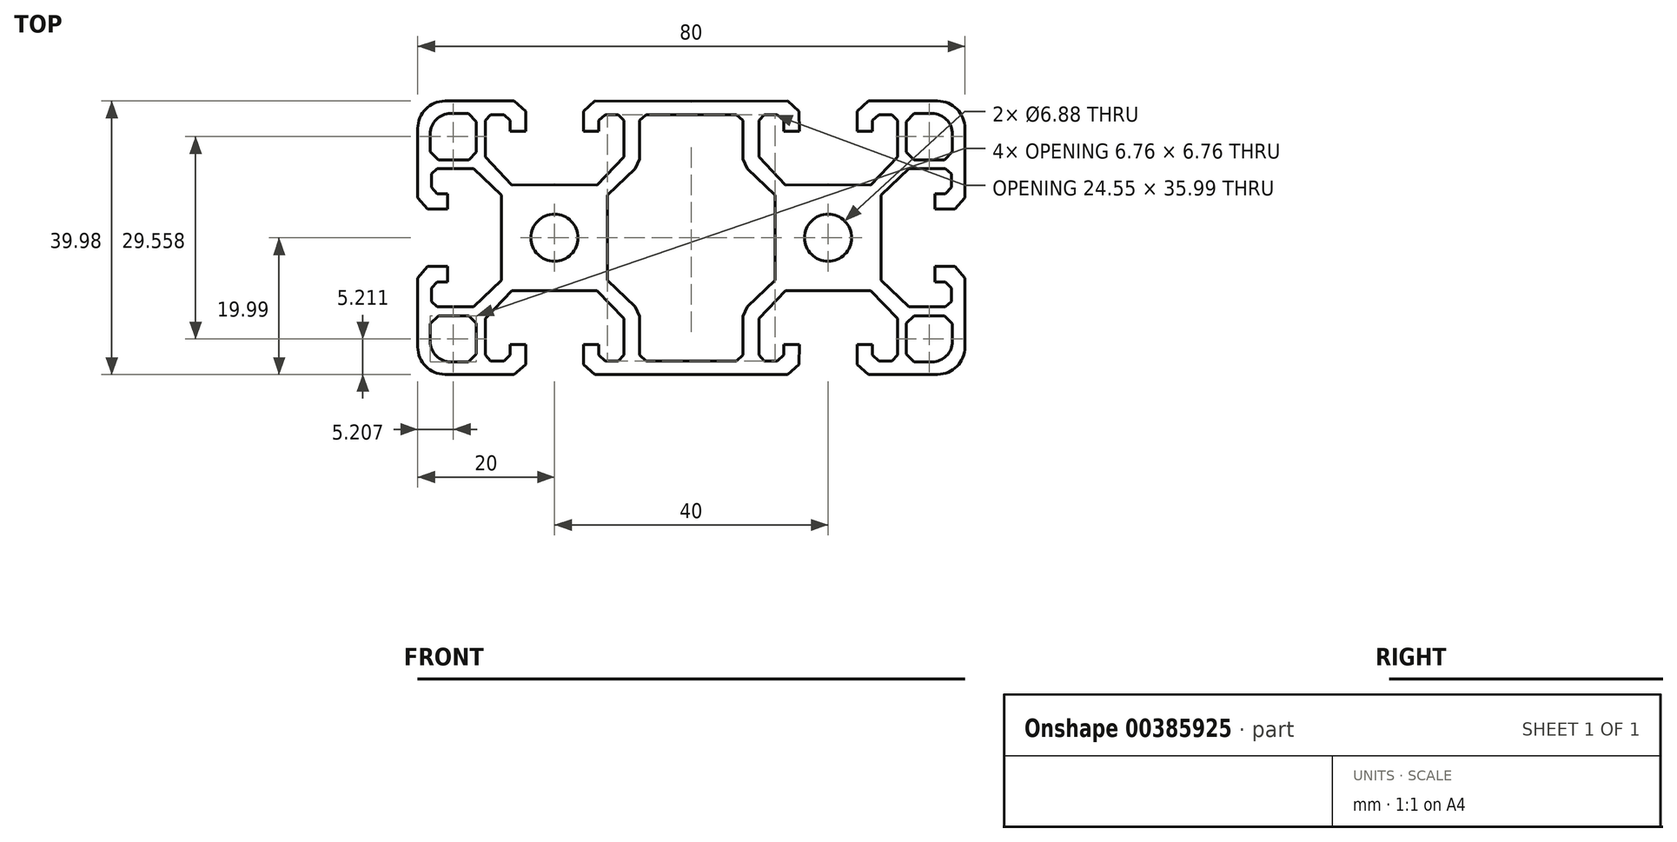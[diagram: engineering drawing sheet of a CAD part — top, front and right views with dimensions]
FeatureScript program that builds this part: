
annotation { "Feature Type Name" : "Feature", "Feature Type Description" : "" }
export const myFeature = defineFeature(function(context is Context, id is Id, definition is map)
    precondition{}
    {
        {
            var Q0;
            Q0=qCreatedBy(makeId("Top.planeOp"),FACE);
            var sketch = newSketch(context, id + "F0", { "sketchPlane" : qUnion([Q0])});
            skLineSegment(sketch, "E0", {"start": v(-150.5, 22.08) * mm, "end": v(-150.5, 75.17) * mm});
            skLineSegment(sketch, "E1", {"start": v(-104.33, 23.38) * mm, "end": v(-104.33, -0.03) * mm});
            skLineSegment(sketch, "E2", {"start": v(-104.33, 23.38) * mm, "end": v(-119.7, 38.04) * mm});
            skLineSegment(sketch, "E3", {"start": v(-119.7, 38.04) * mm, "end": v(-139.74, 38.04) * mm});
            skLineSegment(sketch, "E4", {"start": v(-139.74, 38.04) * mm, "end": v(-143, 35.05) * mm});
            skLineSegment(sketch, "E5", {"start": v(-143, 35.05) * mm, "end": v(-143, 27.8) * mm});
            skLineSegment(sketch, "E6", {"start": v(-143, 27.8) * mm, "end": v(-139.74, 24.28) * mm});
            skLineSegment(sketch, "E7", {"start": v(-139.74, 24.28) * mm, "end": v(-133.95, 24.28) * mm});
            skLineSegment(sketch, "E8", {"start": v(-133.95, 24.28) * mm, "end": v(-133.95, 15.85) * mm});
            skLineSegment(sketch, "E9", {"start": v(-133.95, 15.85) * mm, "end": v(-144.95, 15.85) * mm});
            skLineSegment(sketch, "E10", {"start": v(-144.95, 15.85) * mm, "end": v(-150.5, 22.08) * mm});
            skLineSegment(sketch, "E11", {"start": v(-75.25, 29.07) * mm, "end": v(-75.25, 12.95) * mm, "construction": true});
            skPoint(sketch, "E12", {"position": v(-75.25, 0) * mm});
            skCircle(sketch, "E13", {"center": v(-75.25, 0) * mm, "radius": 12.95 * mm});
            skLineSegment(sketch, "E14", {"start": v(-75.25, 0) * mm, "end": v(-150.5, 75.17) * mm, "construction": true});
            skLineSegment(sketch, "E15", {"start": v(-75.25, 0) * mm, "end": v(-175.7, 0) * mm, "construction": true});
            skLineSegment(sketch, "E16.MirrorCS", {"start": v(-97.41, 75.23) * mm, "end": v(-150.5, 75.17) * mm});
            skLineSegment(sketch, "E17.MirrorCS", {"start": v(-91.18, 69.68) * mm, "end": v(-97.41, 75.23) * mm});
            skLineSegment(sketch, "E18.MirrorCS", {"start": v(-91.17, 58.68) * mm, "end": v(-91.18, 69.68) * mm});
            skLineSegment(sketch, "E19.MirrorCS", {"start": v(-99.6, 58.67) * mm, "end": v(-91.17, 58.68) * mm});
            skLineSegment(sketch, "E20.MirrorCS", {"start": v(-99.6, 64.46) * mm, "end": v(-99.6, 58.67) * mm});
            skLineSegment(sketch, "E21.MirrorCS", {"start": v(-103.12, 67.72) * mm, "end": v(-99.6, 64.46) * mm});
            skLineSegment(sketch, "E22.MirrorCS", {"start": v(-110.38, 67.7) * mm, "end": v(-103.12, 67.72) * mm});
            skLineSegment(sketch, "E23.MirrorCS", {"start": v(-113.37, 64.44) * mm, "end": v(-110.38, 67.7) * mm});
            skLineSegment(sketch, "E24.MirrorCS", {"start": v(-113.34, 44.4) * mm, "end": v(-113.37, 64.44) * mm});
            skLineSegment(sketch, "E25.MirrorCS", {"start": v(-98.66, 29.05) * mm, "end": v(-113.34, 44.4) * mm});
            skLineSegment(sketch, "E26.MirrorCS", {"start": v(-98.66, 29.05) * mm, "end": v(-75.25, 29.07) * mm});
            skLineSegment(sketch, "E27.MirrorCS", {"start": v(-139.74, -38.04) * mm, "end": v(-143, -35.05) * mm});
            skLineSegment(sketch, "E28.MirrorCS", {"start": v(-143, -27.8) * mm, "end": v(-139.74, -24.28) * mm});
            skLineSegment(sketch, "E29.MirrorCS", {"start": v(-139.74, -24.28) * mm, "end": v(-133.95, -24.28) * mm});
            skLineSegment(sketch, "E30.MirrorCS", {"start": v(-144.95, -15.85) * mm, "end": v(-150.5, -22.08) * mm});
            skLineSegment(sketch, "E31.MirrorCS", {"start": v(-104.33, -23.38) * mm, "end": v(-119.7, -38.04) * mm});
            skLineSegment(sketch, "E32.MirrorCS", {"start": v(-97.41, -75.23) * mm, "end": v(-150.5, -75.17) * mm});
            skLineSegment(sketch, "E33.MirrorCS", {"start": v(-119.7, -38.04) * mm, "end": v(-139.74, -38.04) * mm});
            skLineSegment(sketch, "E34.MirrorCS", {"start": v(-150.5, -22.08) * mm, "end": v(-150.5, -75.17) * mm});
            skLineSegment(sketch, "E35.MirrorCS", {"start": v(-133.95, -24.28) * mm, "end": v(-133.95, -15.85) * mm});
            skLineSegment(sketch, "E36.MirrorCS", {"start": v(-143, -35.05) * mm, "end": v(-143, -27.8) * mm});
            skLineSegment(sketch, "E37.MirrorCS", {"start": v(-75.25, 0) * mm, "end": v(-150.5, -75.17) * mm, "construction": true});
            skLineSegment(sketch, "E38.MirrorCS", {"start": v(-133.95, -15.85) * mm, "end": v(-144.95, -15.85) * mm});
            skLineSegment(sketch, "E39.MirrorCS", {"start": v(-99.6, -64.46) * mm, "end": v(-99.6, -58.67) * mm});
            skLineSegment(sketch, "E40.MirrorCS", {"start": v(-113.37, -64.44) * mm, "end": v(-110.38, -67.7) * mm});
            skLineSegment(sketch, "E41.MirrorCS", {"start": v(-103.12, -67.72) * mm, "end": v(-99.6, -64.46) * mm});
            skLineSegment(sketch, "E42.MirrorCS", {"start": v(-98.66, -29.05) * mm, "end": v(-75.25, -29.07) * mm});
            skLineSegment(sketch, "E43.MirrorCS", {"start": v(-99.6, -58.67) * mm, "end": v(-91.17, -58.68) * mm});
            skLineSegment(sketch, "E44.MirrorCS", {"start": v(-91.18, -69.68) * mm, "end": v(-97.41, -75.23) * mm});
            skLineSegment(sketch, "E45.MirrorCS", {"start": v(-98.66, -29.05) * mm, "end": v(-113.34, -44.4) * mm});
            skLineSegment(sketch, "E46.MirrorCS", {"start": v(-110.38, -67.7) * mm, "end": v(-103.12, -67.72) * mm});
            skLineSegment(sketch, "E47.MirrorCS", {"start": v(-91.17, -58.68) * mm, "end": v(-91.18, -69.68) * mm});
            skLineSegment(sketch, "E48.MirrorCS", {"start": v(-113.34, -44.4) * mm, "end": v(-113.37, -64.44) * mm});
            skLineSegment(sketch, "E49.MirrorCS", {"start": v(-51.84, 29.05) * mm, "end": v(-75.25, 29.07) * mm});
            skLineSegment(sketch, "E50.MirrorCS", {"start": v(-51.84, 29.05) * mm, "end": v(-37.16, 44.4) * mm});
            skLineSegment(sketch, "E51.MirrorCS", {"start": v(-37.16, 44.4) * mm, "end": v(-37.14, 64.44) * mm});
            skLineSegment(sketch, "E52.MirrorCS", {"start": v(-40.13, 67.7) * mm, "end": v(-47.39, 67.72) * mm});
            skLineSegment(sketch, "E53.MirrorCS", {"start": v(-47.39, 67.72) * mm, "end": v(-50.9, 64.46) * mm});
            skLineSegment(sketch, "E54.MirrorCS", {"start": v(-59.33, 69.68) * mm, "end": v(-53.1, 75.23) * mm});
            skLineSegment(sketch, "E55.MirrorCS", {"start": v(-50.91, 58.67) * mm, "end": v(-59.34, 58.68) * mm});
            skLineSegment(sketch, "E56.MirrorCS", {"start": v(-53.1, 75.23) * mm, "end": v(0, 75.17) * mm});
            skLineSegment(sketch, "E57.MirrorCS", {"start": v(-59.34, 58.68) * mm, "end": v(-59.33, 69.68) * mm});
            skLineSegment(sketch, "E58.MirrorCS", {"start": v(-50.9, 64.46) * mm, "end": v(-50.91, 58.67) * mm});
            skLineSegment(sketch, "E59.MirrorCS", {"start": v(-37.14, 64.44) * mm, "end": v(-40.13, 67.7) * mm});
            skLineSegment(sketch, "E60.MirrorCS", {"start": v(-51.84, -29.05) * mm, "end": v(-75.25, -29.07) * mm});
            skLineSegment(sketch, "E61.MirrorCS", {"start": v(-51.84, -29.05) * mm, "end": v(-37.16, -44.4) * mm});
            skLineSegment(sketch, "E62.MirrorCS", {"start": v(-37.16, -44.4) * mm, "end": v(-37.14, -64.44) * mm});
            skLineSegment(sketch, "E63.MirrorCS", {"start": v(-37.14, -64.44) * mm, "end": v(-40.13, -67.7) * mm});
            skLineSegment(sketch, "E64.MirrorCS", {"start": v(-40.13, -67.7) * mm, "end": v(-47.39, -67.72) * mm});
            skLineSegment(sketch, "E65.MirrorCS", {"start": v(-47.39, -67.72) * mm, "end": v(-50.9, -64.46) * mm});
            skLineSegment(sketch, "E66.MirrorCS", {"start": v(-50.9, -64.46) * mm, "end": v(-50.91, -58.67) * mm});
            skLineSegment(sketch, "E67.MirrorCS", {"start": v(-50.91, -58.67) * mm, "end": v(-59.34, -58.68) * mm});
            skLineSegment(sketch, "E68.MirrorCS", {"start": v(-59.34, -58.68) * mm, "end": v(-59.33, -69.68) * mm});
            skLineSegment(sketch, "E69.MirrorCS", {"start": v(-59.33, -69.68) * mm, "end": v(-53.1, -75.23) * mm});
            skLineSegment(sketch, "E70.MirrorCS", {"start": v(-53.1, -75.23) * mm, "end": v(0, -75.17) * mm});
            skLineSegment(sketch, "E71", {"start": v(-120.32, 45.02) * mm, "end": v(-122.44, 42.9) * mm});
            skLineSegment(sketch, "E72", {"start": v(-122.44, 42.9) * mm, "end": v(-139.2, 42.9) * mm});
            skLineSegment(sketch, "E73", {"start": v(-139.2, 42.9) * mm, "end": v(-143.63, 47.32) * mm});
            skLineSegment(sketch, "E74", {"start": v(-143.63, 47.32) * mm, "end": v(-143.63, 68.3) * mm});
            skLineSegment(sketch, "E75.MirrorCS", {"start": v(-120.32, 45.02) * mm, "end": v(-118.2, 47.14) * mm});
            skLineSegment(sketch, "E76.MirrorCS", {"start": v(-118.2, 47.14) * mm, "end": v(-118.22, 63.9) * mm});
            skLineSegment(sketch, "E77.MirrorCS", {"start": v(-118.22, 63.9) * mm, "end": v(-122.65, 68.32) * mm});
            skLineSegment(sketch, "E78.MirrorCS", {"start": v(-122.65, 68.32) * mm, "end": v(-143.63, 68.3) * mm});
            skLineSegment(sketch, "E79.MirrorCS", {"start": v(-122.44, -42.9) * mm, "end": v(-139.2, -42.9) * mm});
            skLineSegment(sketch, "E80.MirrorCS", {"start": v(-120.32, -45.02) * mm, "end": v(-122.44, -42.9) * mm});
            skLineSegment(sketch, "E81.MirrorCS", {"start": v(-120.32, -45.02) * mm, "end": v(-118.2, -47.14) * mm});
            skLineSegment(sketch, "E82.MirrorCS", {"start": v(-118.2, -47.14) * mm, "end": v(-118.22, -63.9) * mm});
            skLineSegment(sketch, "E83.MirrorCS", {"start": v(-118.22, -63.9) * mm, "end": v(-122.65, -68.32) * mm});
            skLineSegment(sketch, "E84.MirrorCS", {"start": v(-122.65, -68.32) * mm, "end": v(-143.63, -68.3) * mm});
            skLineSegment(sketch, "E85.MirrorCS", {"start": v(-143.63, -47.32) * mm, "end": v(-143.63, -68.3) * mm});
            skLineSegment(sketch, "E86.MirrorCS", {"start": v(-139.2, -42.9) * mm, "end": v(-143.63, -47.32) * mm});
            skLineSegment(sketch, "E87.MirrorCS", {"start": v(-104.33, -23.38) * mm, "end": v(-104.33, 0.03) * mm});
            skLineSegment(sketch, "E88", {"start": v(0, 75.17) * mm, "end": v(0, -75.17) * mm, "construction": true});
            skLineSegment(sketch, "E89.MirrorCS", {"start": v(-46.18, 23.38) * mm, "end": v(-30.82, 38.04) * mm});
            skLineSegment(sketch, "E90.MirrorCS", {"start": v(-46.18, 23.38) * mm, "end": v(-46.18, -0.03) * mm});
            skLineSegment(sketch, "E91.MirrorCS", {"start": v(-46.18, -23.38) * mm, "end": v(-46.18, 0.03) * mm});
            skLineSegment(sketch, "E92.MirrorCS", {"start": v(-46.18, -23.38) * mm, "end": v(-30.82, -38.04) * mm});
            skLineSegment(sketch, "E93", {"start": v(-30.82, 38.04) * mm, "end": v(-28.34, 43.24) * mm});
            skLineSegment(sketch, "E94", {"start": v(-28.34, 43.24) * mm, "end": v(-28.34, 64.44) * mm});
            skLineSegment(sketch, "E95", {"start": v(-28.34, 64.44) * mm, "end": v(-24.77, 67.7) * mm});
            skLineSegment(sketch, "E96", {"start": v(-24.77, 67.7) * mm, "end": v(0, 67.7) * mm});
            skLineSegment(sketch, "E97.MirrorCS", {"start": v(-30.82, -38.04) * mm, "end": v(-28.34, -43.24) * mm});
            skLineSegment(sketch, "E98.MirrorCS", {"start": v(-28.34, -43.24) * mm, "end": v(-28.34, -64.44) * mm});
            skLineSegment(sketch, "E99.MirrorCS", {"start": v(-24.77, -67.7) * mm, "end": v(0, -67.7) * mm});
            skLineSegment(sketch, "E100.MirrorCS", {"start": v(-28.34, -64.44) * mm, "end": v(-24.77, -67.7) * mm});
            skLineSegment(sketch, "E101.MirrorCS", {"start": v(139.74, -38.04) * mm, "end": v(143, -35.05) * mm});
            skLineSegment(sketch, "E102.MirrorCS", {"start": v(50.9, -64.46) * mm, "end": v(50.91, -58.67) * mm});
            skLineSegment(sketch, "E103.MirrorCS", {"start": v(110.38, 67.7) * mm, "end": v(103.12, 67.72) * mm});
            skLineSegment(sketch, "E104.MirrorCS", {"start": v(30.82, -38.04) * mm, "end": v(28.34, -43.24) * mm});
            skLineSegment(sketch, "E105.MirrorCS", {"start": v(120.32, 45.02) * mm, "end": v(118.2, 47.14) * mm});
            skLineSegment(sketch, "E106.MirrorCS", {"start": v(37.14, 64.44) * mm, "end": v(40.13, 67.7) * mm});
            skLineSegment(sketch, "E107.MirrorCS", {"start": v(50.9, 64.46) * mm, "end": v(50.91, 58.67) * mm});
            skLineSegment(sketch, "E108.MirrorCS", {"start": v(103.12, 67.72) * mm, "end": v(99.6, 64.46) * mm});
            skLineSegment(sketch, "E109.MirrorCS", {"start": v(120.32, -45.02) * mm, "end": v(118.2, -47.14) * mm});
            skLineSegment(sketch, "E110.MirrorCS", {"start": v(139.2, 42.9) * mm, "end": v(143.63, 47.32) * mm});
            skLineSegment(sketch, "E111.MirrorCS", {"start": v(40.13, 67.7) * mm, "end": v(47.39, 67.72) * mm});
            skLineSegment(sketch, "E112.MirrorCS", {"start": v(139.74, 24.28) * mm, "end": v(133.95, 24.28) * mm});
            skLineSegment(sketch, "E113.MirrorCS", {"start": v(139.2, -42.9) * mm, "end": v(143.63, -47.32) * mm});
            skLineSegment(sketch, "E114.MirrorCS", {"start": v(103.12, -67.72) * mm, "end": v(99.6, -64.46) * mm});
            skLineSegment(sketch, "E115.MirrorCS", {"start": v(144.95, -15.85) * mm, "end": v(150.5, -22.08) * mm});
            skLineSegment(sketch, "E116.MirrorCS", {"start": v(59.33, 69.68) * mm, "end": v(53.1, 75.23) * mm});
            skLineSegment(sketch, "E117.MirrorCS", {"start": v(139.74, -24.28) * mm, "end": v(133.95, -24.28) * mm});
            skLineSegment(sketch, "E118.MirrorCS", {"start": v(143, 27.8) * mm, "end": v(139.74, 24.28) * mm});
            skLineSegment(sketch, "E119.MirrorCS", {"start": v(118.22, 63.9) * mm, "end": v(122.65, 68.32) * mm});
            skLineSegment(sketch, "E120.MirrorCS", {"start": v(110.38, -67.7) * mm, "end": v(103.12, -67.72) * mm});
            skLineSegment(sketch, "E121.MirrorCS", {"start": v(143, -35.05) * mm, "end": v(143, -27.8) * mm});
            skLineSegment(sketch, "E122.MirrorCS", {"start": v(120.32, -45.02) * mm, "end": v(122.44, -42.9) * mm});
            skLineSegment(sketch, "E123.MirrorCS", {"start": v(99.6, 64.46) * mm, "end": v(99.6, 58.67) * mm});
            skLineSegment(sketch, "E124.MirrorCS", {"start": v(40.13, -67.7) * mm, "end": v(47.39, -67.72) * mm});
            skLineSegment(sketch, "E125.MirrorCS", {"start": v(47.39, -67.72) * mm, "end": v(50.9, -64.46) * mm});
            skLineSegment(sketch, "E126.MirrorCS", {"start": v(91.18, 69.68) * mm, "end": v(97.41, 75.23) * mm});
            skLineSegment(sketch, "E127.MirrorCS", {"start": v(28.34, 64.44) * mm, "end": v(24.77, 67.7) * mm});
            skLineSegment(sketch, "E128.MirrorCS", {"start": v(113.37, -64.44) * mm, "end": v(110.38, -67.7) * mm});
            skLineSegment(sketch, "E129.MirrorCS", {"start": v(37.14, -64.44) * mm, "end": v(40.13, -67.7) * mm});
            skLineSegment(sketch, "E130.MirrorCS", {"start": v(144.95, 15.85) * mm, "end": v(150.5, 22.08) * mm});
            skLineSegment(sketch, "E131.MirrorCS", {"start": v(91.18, -69.68) * mm, "end": v(97.41, -75.23) * mm});
            skLineSegment(sketch, "E132.MirrorCS", {"start": v(143, 35.05) * mm, "end": v(143, 27.8) * mm});
            skLineSegment(sketch, "E133.MirrorCS", {"start": v(133.95, 24.28) * mm, "end": v(133.95, 15.85) * mm});
            skLineSegment(sketch, "E134.MirrorCS", {"start": v(99.6, -64.46) * mm, "end": v(99.6, -58.67) * mm});
            skLineSegment(sketch, "E135.MirrorCS", {"start": v(59.33, -69.68) * mm, "end": v(53.1, -75.23) * mm});
            skLineSegment(sketch, "E136.MirrorCS", {"start": v(139.74, 38.04) * mm, "end": v(143, 35.05) * mm});
            skLineSegment(sketch, "E137.MirrorCS", {"start": v(47.39, 67.72) * mm, "end": v(50.9, 64.46) * mm});
            skLineSegment(sketch, "E138.MirrorCS", {"start": v(99.6, -58.67) * mm, "end": v(91.17, -58.68) * mm});
            skLineSegment(sketch, "E139.MirrorCS", {"start": v(113.37, 64.44) * mm, "end": v(110.38, 67.7) * mm});
            skLineSegment(sketch, "E140.MirrorCS", {"start": v(50.91, -58.67) * mm, "end": v(59.34, -58.68) * mm});
            skLineSegment(sketch, "E141.MirrorCS", {"start": v(30.82, 38.04) * mm, "end": v(28.34, 43.24) * mm});
            skLineSegment(sketch, "E142.MirrorCS", {"start": v(120.32, 45.02) * mm, "end": v(122.44, 42.9) * mm});
            skLineSegment(sketch, "E143.MirrorCS", {"start": v(99.6, 58.67) * mm, "end": v(91.17, 58.68) * mm});
            skLineSegment(sketch, "E144.MirrorCS", {"start": v(143, -27.8) * mm, "end": v(139.74, -24.28) * mm});
            skLineSegment(sketch, "E145.MirrorCS", {"start": v(28.34, -64.44) * mm, "end": v(24.77, -67.7) * mm});
            skLineSegment(sketch, "E146.MirrorCS", {"start": v(118.22, -63.9) * mm, "end": v(122.65, -68.32) * mm});
            skLineSegment(sketch, "E147.MirrorCS", {"start": v(133.95, -24.28) * mm, "end": v(133.95, -15.85) * mm});
            skLineSegment(sketch, "E148.MirrorCS", {"start": v(50.91, 58.67) * mm, "end": v(59.34, 58.68) * mm});
            skLineSegment(sketch, "E149.MirrorCS", {"start": v(104.33, -23.38) * mm, "end": v(119.7, -38.04) * mm});
            skLineSegment(sketch, "E150.MirrorCS", {"start": v(97.41, -75.23) * mm, "end": v(150.5, -75.17) * mm});
            skLineSegment(sketch, "E151.MirrorCS", {"start": v(75.25, 0) * mm, "end": v(150.5, -75.17) * mm, "construction": true});
            skLineSegment(sketch, "E152.MirrorCS", {"start": v(119.7, -38.04) * mm, "end": v(139.74, -38.04) * mm});
            skLineSegment(sketch, "E153.MirrorCS", {"start": v(104.33, -23.38) * mm, "end": v(104.33, 0.03) * mm});
            skLineSegment(sketch, "E154.MirrorCS", {"start": v(51.84, 29.05) * mm, "end": v(37.16, 44.4) * mm});
            skLineSegment(sketch, "E155.MirrorCS", {"start": v(133.95, -15.85) * mm, "end": v(144.95, -15.85) * mm});
            skLineSegment(sketch, "E156.MirrorCS", {"start": v(118.2, -47.14) * mm, "end": v(118.22, -63.9) * mm});
            skLineSegment(sketch, "E157.MirrorCS", {"start": v(75.25, 0) * mm, "end": v(175.7, 0) * mm, "construction": true});
            skPoint(sketch, "E158.MirrorP", {"position": v(75.25, 0) * mm});
            skLineSegment(sketch, "E159.MirrorCS", {"start": v(46.18, 23.38) * mm, "end": v(46.18, -0.03) * mm});
            skLineSegment(sketch, "E160.MirrorCS", {"start": v(98.66, -29.05) * mm, "end": v(113.34, -44.4) * mm});
            skLineSegment(sketch, "E161.MirrorCS", {"start": v(46.18, 23.38) * mm, "end": v(30.82, 38.04) * mm});
            skLineSegment(sketch, "E162.MirrorCS", {"start": v(143.63, 47.32) * mm, "end": v(143.63, 68.3) * mm});
            skLineSegment(sketch, "E163.MirrorCS", {"start": v(150.5, 22.08) * mm, "end": v(150.5, 75.17) * mm});
            skLineSegment(sketch, "E164.MirrorCS", {"start": v(28.34, -43.24) * mm, "end": v(28.34, -64.44) * mm});
            skLineSegment(sketch, "E165.MirrorCS", {"start": v(133.95, 15.85) * mm, "end": v(144.95, 15.85) * mm});
            skLineSegment(sketch, "E166.MirrorCS", {"start": v(104.33, 23.38) * mm, "end": v(104.33, -0.03) * mm});
            skLineSegment(sketch, "E167.MirrorCS", {"start": v(59.34, -58.68) * mm, "end": v(59.33, -69.68) * mm});
            skLineSegment(sketch, "E168.MirrorCS", {"start": v(98.66, 29.05) * mm, "end": v(75.25, 29.07) * mm});
            skCircle(sketch, "E169.MirrorC", {"center": v(75.25, 0) * mm, "radius": 12.95 * mm});
            skLineSegment(sketch, "E170.MirrorCS", {"start": v(91.17, -58.68) * mm, "end": v(91.18, -69.68) * mm});
            skLineSegment(sketch, "E171.MirrorCS", {"start": v(113.34, -44.4) * mm, "end": v(113.37, -64.44) * mm});
            skLineSegment(sketch, "E172.MirrorCS", {"start": v(46.18, -23.38) * mm, "end": v(30.82, -38.04) * mm});
            skLineSegment(sketch, "E173.MirrorCS", {"start": v(51.84, 29.05) * mm, "end": v(75.25, 29.07) * mm});
            skLineSegment(sketch, "E174.MirrorCS", {"start": v(75.25, 0) * mm, "end": v(150.5, 75.17) * mm, "construction": true});
            skLineSegment(sketch, "E175.MirrorCS", {"start": v(51.84, -29.05) * mm, "end": v(37.16, -44.4) * mm});
            skLineSegment(sketch, "E176.MirrorCS", {"start": v(24.77, -67.7) * mm, "end": v(0, -67.7) * mm});
            skLineSegment(sketch, "E177.MirrorCS", {"start": v(37.16, 44.4) * mm, "end": v(37.14, 64.44) * mm});
            skLineSegment(sketch, "E178.MirrorCS", {"start": v(51.84, -29.05) * mm, "end": v(75.25, -29.07) * mm});
            skLineSegment(sketch, "E179.MirrorCS", {"start": v(113.34, 44.4) * mm, "end": v(113.37, 64.44) * mm});
            skLineSegment(sketch, "E180.MirrorCS", {"start": v(24.77, 67.7) * mm, "end": v(0, 67.7) * mm});
            skLineSegment(sketch, "E181.MirrorCS", {"start": v(53.1, -75.23) * mm, "end": v(0, -75.17) * mm});
            skLineSegment(sketch, "E182.MirrorCS", {"start": v(75.25, 29.07) * mm, "end": v(75.25, 12.95) * mm, "construction": true});
            skLineSegment(sketch, "E183.MirrorCS", {"start": v(97.41, 75.23) * mm, "end": v(150.5, 75.17) * mm});
            skLineSegment(sketch, "E184.MirrorCS", {"start": v(122.65, -68.32) * mm, "end": v(143.63, -68.3) * mm});
            skLineSegment(sketch, "E185.MirrorCS", {"start": v(122.44, -42.9) * mm, "end": v(139.2, -42.9) * mm});
            skLineSegment(sketch, "E186.MirrorCS", {"start": v(98.66, -29.05) * mm, "end": v(75.25, -29.07) * mm});
            skLineSegment(sketch, "E187.MirrorCS", {"start": v(46.18, -23.38) * mm, "end": v(46.18, 0.03) * mm});
            skLineSegment(sketch, "E188.MirrorCS", {"start": v(91.17, 58.68) * mm, "end": v(91.18, 69.68) * mm});
            skLineSegment(sketch, "E189.MirrorCS", {"start": v(122.65, 68.32) * mm, "end": v(143.63, 68.3) * mm});
            skLineSegment(sketch, "E190.MirrorCS", {"start": v(59.34, 58.68) * mm, "end": v(59.33, 69.68) * mm});
            skLineSegment(sketch, "E191.MirrorCS", {"start": v(53.1, 75.23) * mm, "end": v(0, 75.17) * mm});
            skLineSegment(sketch, "E192.MirrorCS", {"start": v(37.16, -44.4) * mm, "end": v(37.14, -64.44) * mm});
            skLineSegment(sketch, "E193.MirrorCS", {"start": v(104.33, 23.38) * mm, "end": v(119.7, 38.04) * mm});
            skLineSegment(sketch, "E194.MirrorCS", {"start": v(119.7, 38.04) * mm, "end": v(139.74, 38.04) * mm});
            skLineSegment(sketch, "E195.MirrorCS", {"start": v(28.34, 43.24) * mm, "end": v(28.34, 64.44) * mm});
            skLineSegment(sketch, "E196.MirrorCS", {"start": v(122.44, 42.9) * mm, "end": v(139.2, 42.9) * mm});
            skLineSegment(sketch, "E197.MirrorCS", {"start": v(118.2, 47.14) * mm, "end": v(118.22, 63.9) * mm});
            skLineSegment(sketch, "E198.MirrorCS", {"start": v(98.66, 29.05) * mm, "end": v(113.34, 44.4) * mm});
            skLineSegment(sketch, "E199.MirrorCS", {"start": v(150.5, -22.08) * mm, "end": v(150.5, -75.17) * mm});
            skLineSegment(sketch, "E200.MirrorCS", {"start": v(143.63, -47.32) * mm, "end": v(143.63, -68.3) * mm});
            skPoint(sketch, "E201.visualSharp", {"position": v(-150.5, 75.17) * mm});
            skLineSegment(sketch, "E201.filletArc", {"start": v(-575.32, 265.37) * mm, "end": v(-575.32, 265.37) * mm});
            skSolve(sketch);
        }
        {
            var Q0;
            Q0=makeQuery(id+"F0.imprint","IMPRINT",FACE,{"disambiguationData":[TD([[makeQuery(id+"F0.imprint","IMPRINT",EDGE,{"derivedFrom":sQuery(id+"F0.wireOp",EDGE,"E0")}),-1.0]])]});
            extrude(context, id + "F1", {"entities" : qUnion([Q0]), "depth" : 0 * mm, "offsetDistance" : 25 * mm});
        }
        {
            var Q0;
            Q0=makeQuery(id+"F1.opExtrude","SWEPT_BODY",BODY,{"disambiguationData":[OSD([sQuery(id+"F0.wireOp",EDGE,"E0"),sQuery(id+"F0.wireOp",EDGE,"E1"),sQuery(id+"F0.wireOp",EDGE,"E2"),sQuery(id+"F0.wireOp",EDGE,"E3"),sQuery(id+"F0.wireOp",EDGE,"E4"),sQuery(id+"F0.wireOp",EDGE,"E5"),sQuery(id+"F0.wireOp",EDGE,"E6"),sQuery(id+"F0.wireOp",EDGE,"E7"),sQuery(id+"F0.wireOp",EDGE,"E8"),sQuery(id+"F0.wireOp",EDGE,"E9"),sQuery(id+"F0.wireOp",EDGE,"E10"),sQuery(id+"F0.wireOp",EDGE,"E13"),sQuery(id+"F0.wireOp",EDGE,"E16.MirrorCS"),sQuery(id+"F0.wireOp",EDGE,"E17.MirrorCS"),sQuery(id+"F0.wireOp",EDGE,"E18.MirrorCS"),sQuery(id+"F0.wireOp",EDGE,"E19.MirrorCS"),sQuery(id+"F0.wireOp",EDGE,"E20.MirrorCS"),sQuery(id+"F0.wireOp",EDGE,"E21.MirrorCS"),sQuery(id+"F0.wireOp",EDGE,"E22.MirrorCS"),sQuery(id+"F0.wireOp",EDGE,"E23.MirrorCS"),sQuery(id+"F0.wireOp",EDGE,"E24.MirrorCS"),sQuery(id+"F0.wireOp",EDGE,"E25.MirrorCS"),sQuery(id+"F0.wireOp",EDGE,"E26.MirrorCS"),sQuery(id+"F0.wireOp",EDGE,"E27.MirrorCS"),sQuery(id+"F0.wireOp",EDGE,"E28.MirrorCS"),sQuery(id+"F0.wireOp",EDGE,"E29.MirrorCS"),sQuery(id+"F0.wireOp",EDGE,"E30.MirrorCS"),sQuery(id+"F0.wireOp",EDGE,"E34.MirrorCS"),sQuery(id+"F0.wireOp",EDGE,"E35.MirrorCS"),sQuery(id+"F0.wireOp",EDGE,"E36.MirrorCS"),sQuery(id+"F0.wireOp",EDGE,"E38.MirrorCS"),sQuery(id+"F0.wireOp",EDGE,"E39.MirrorCS"),sQuery(id+"F0.wireOp",EDGE,"E40.MirrorCS"),sQuery(id+"F0.wireOp",EDGE,"E33.MirrorCS"),sQuery(id+"F0.wireOp",EDGE,"E41.MirrorCS"),sQuery(id+"F0.wireOp",EDGE,"E42.MirrorCS"),sQuery(id+"F0.wireOp",EDGE,"E43.MirrorCS"),sQuery(id+"F0.wireOp",EDGE,"E44.MirrorCS"),sQuery(id+"F0.wireOp",EDGE,"E45.MirrorCS"),sQuery(id+"F0.wireOp",EDGE,"E46.MirrorCS"),sQuery(id+"F0.wireOp",EDGE,"E47.MirrorCS"),sQuery(id+"F0.wireOp",EDGE,"E32.MirrorCS"),sQuery(id+"F0.wireOp",EDGE,"E31.MirrorCS"),sQuery(id+"F0.wireOp",EDGE,"E48.MirrorCS"),sQuery(id+"F0.wireOp",EDGE,"E49.MirrorCS"),sQuery(id+"F0.wireOp",EDGE,"E50.MirrorCS"),sQuery(id+"F0.wireOp",EDGE,"E51.MirrorCS"),sQuery(id+"F0.wireOp",EDGE,"E52.MirrorCS"),sQuery(id+"F0.wireOp",EDGE,"E53.MirrorCS"),sQuery(id+"F0.wireOp",EDGE,"E54.MirrorCS"),sQuery(id+"F0.wireOp",EDGE,"E55.MirrorCS"),sQuery(id+"F0.wireOp",EDGE,"E56.MirrorCS"),sQuery(id+"F0.wireOp",EDGE,"E57.MirrorCS"),sQuery(id+"F0.wireOp",EDGE,"E58.MirrorCS"),sQuery(id+"F0.wireOp",EDGE,"E59.MirrorCS"),sQuery(id+"F0.wireOp",EDGE,"E60.MirrorCS"),sQuery(id+"F0.wireOp",EDGE,"E61.MirrorCS"),sQuery(id+"F0.wireOp",EDGE,"E62.MirrorCS"),sQuery(id+"F0.wireOp",EDGE,"E63.MirrorCS"),sQuery(id+"F0.wireOp",EDGE,"E64.MirrorCS"),sQuery(id+"F0.wireOp",EDGE,"E65.MirrorCS"),sQuery(id+"F0.wireOp",EDGE,"E66.MirrorCS"),sQuery(id+"F0.wireOp",EDGE,"E67.MirrorCS"),sQuery(id+"F0.wireOp",EDGE,"E68.MirrorCS"),sQuery(id+"F0.wireOp",EDGE,"E69.MirrorCS"),sQuery(id+"F0.wireOp",EDGE,"E70.MirrorCS"),sQuery(id+"F0.wireOp",EDGE,"E71"),sQuery(id+"F0.wireOp",EDGE,"E72"),sQuery(id+"F0.wireOp",EDGE,"E73"),sQuery(id+"F0.wireOp",EDGE,"E74"),sQuery(id+"F0.wireOp",EDGE,"E75.MirrorCS"),sQuery(id+"F0.wireOp",EDGE,"E76.MirrorCS"),sQuery(id+"F0.wireOp",EDGE,"E77.MirrorCS"),sQuery(id+"F0.wireOp",EDGE,"E78.MirrorCS"),sQuery(id+"F0.wireOp",EDGE,"E79.MirrorCS"),sQuery(id+"F0.wireOp",EDGE,"E80.MirrorCS"),sQuery(id+"F0.wireOp",EDGE,"E81.MirrorCS"),sQuery(id+"F0.wireOp",EDGE,"E82.MirrorCS"),sQuery(id+"F0.wireOp",EDGE,"E83.MirrorCS"),sQuery(id+"F0.wireOp",EDGE,"E84.MirrorCS"),sQuery(id+"F0.wireOp",EDGE,"E85.MirrorCS"),sQuery(id+"F0.wireOp",EDGE,"E86.MirrorCS"),sQuery(id+"F0.wireOp",EDGE,"E87.MirrorCS"),sQuery(id+"F0.wireOp",EDGE,"E89.MirrorCS"),sQuery(id+"F0.wireOp",EDGE,"E90.MirrorCS"),sQuery(id+"F0.wireOp",EDGE,"E91.MirrorCS"),sQuery(id+"F0.wireOp",EDGE,"E92.MirrorCS"),sQuery(id+"F0.wireOp",EDGE,"E93"),sQuery(id+"F0.wireOp",EDGE,"E94"),sQuery(id+"F0.wireOp",EDGE,"E95"),sQuery(id+"F0.wireOp",EDGE,"E96"),sQuery(id+"F0.wireOp",EDGE,"E97.MirrorCS"),sQuery(id+"F0.wireOp",EDGE,"E98.MirrorCS"),sQuery(id+"F0.wireOp",EDGE,"E99.MirrorCS"),sQuery(id+"F0.wireOp",EDGE,"E100.MirrorCS"),sQuery(id+"F0.wireOp",EDGE,"E101.MirrorCS"),sQuery(id+"F0.wireOp",EDGE,"E102.MirrorCS"),sQuery(id+"F0.wireOp",EDGE,"E103.MirrorCS"),sQuery(id+"F0.wireOp",EDGE,"E104.MirrorCS"),sQuery(id+"F0.wireOp",EDGE,"E105.MirrorCS"),sQuery(id+"F0.wireOp",EDGE,"E106.MirrorCS"),sQuery(id+"F0.wireOp",EDGE,"E107.MirrorCS"),sQuery(id+"F0.wireOp",EDGE,"E108.MirrorCS"),sQuery(id+"F0.wireOp",EDGE,"E109.MirrorCS"),sQuery(id+"F0.wireOp",EDGE,"E110.MirrorCS"),sQuery(id+"F0.wireOp",EDGE,"E111.MirrorCS"),sQuery(id+"F0.wireOp",EDGE,"E112.MirrorCS"),sQuery(id+"F0.wireOp",EDGE,"E113.MirrorCS"),sQuery(id+"F0.wireOp",EDGE,"E114.MirrorCS"),sQuery(id+"F0.wireOp",EDGE,"E115.MirrorCS"),sQuery(id+"F0.wireOp",EDGE,"E116.MirrorCS"),sQuery(id+"F0.wireOp",EDGE,"E117.MirrorCS"),sQuery(id+"F0.wireOp",EDGE,"E118.MirrorCS"),sQuery(id+"F0.wireOp",EDGE,"E119.MirrorCS"),sQuery(id+"F0.wireOp",EDGE,"E120.MirrorCS"),sQuery(id+"F0.wireOp",EDGE,"E121.MirrorCS"),sQuery(id+"F0.wireOp",EDGE,"E122.MirrorCS"),sQuery(id+"F0.wireOp",EDGE,"E123.MirrorCS"),sQuery(id+"F0.wireOp",EDGE,"E124.MirrorCS"),sQuery(id+"F0.wireOp",EDGE,"E125.MirrorCS"),sQuery(id+"F0.wireOp",EDGE,"E126.MirrorCS"),sQuery(id+"F0.wireOp",EDGE,"E127.MirrorCS"),sQuery(id+"F0.wireOp",EDGE,"E128.MirrorCS"),sQuery(id+"F0.wireOp",EDGE,"E129.MirrorCS"),sQuery(id+"F0.wireOp",EDGE,"E130.MirrorCS"),sQuery(id+"F0.wireOp",EDGE,"E131.MirrorCS"),sQuery(id+"F0.wireOp",EDGE,"E132.MirrorCS"),sQuery(id+"F0.wireOp",EDGE,"E133.MirrorCS"),sQuery(id+"F0.wireOp",EDGE,"E134.MirrorCS"),sQuery(id+"F0.wireOp",EDGE,"E135.MirrorCS"),sQuery(id+"F0.wireOp",EDGE,"E136.MirrorCS"),sQuery(id+"F0.wireOp",EDGE,"E137.MirrorCS"),sQuery(id+"F0.wireOp",EDGE,"E138.MirrorCS"),sQuery(id+"F0.wireOp",EDGE,"E139.MirrorCS"),sQuery(id+"F0.wireOp",EDGE,"E140.MirrorCS"),sQuery(id+"F0.wireOp",EDGE,"E141.MirrorCS"),sQuery(id+"F0.wireOp",EDGE,"E142.MirrorCS"),sQuery(id+"F0.wireOp",EDGE,"E143.MirrorCS"),sQuery(id+"F0.wireOp",EDGE,"E144.MirrorCS"),sQuery(id+"F0.wireOp",EDGE,"E145.MirrorCS"),sQuery(id+"F0.wireOp",EDGE,"E146.MirrorCS"),sQuery(id+"F0.wireOp",EDGE,"E147.MirrorCS"),sQuery(id+"F0.wireOp",EDGE,"E148.MirrorCS"),sQuery(id+"F0.wireOp",EDGE,"E154.MirrorCS"),sQuery(id+"F0.wireOp",EDGE,"E155.MirrorCS"),sQuery(id+"F0.wireOp",EDGE,"E156.MirrorCS"),sQuery(id+"F0.wireOp",EDGE,"E159.MirrorCS"),sQuery(id+"F0.wireOp",EDGE,"E160.MirrorCS"),sQuery(id+"F0.wireOp",EDGE,"E161.MirrorCS"),sQuery(id+"F0.wireOp",EDGE,"E162.MirrorCS"),sQuery(id+"F0.wireOp",EDGE,"E163.MirrorCS"),sQuery(id+"F0.wireOp",EDGE,"E164.MirrorCS"),sQuery(id+"F0.wireOp",EDGE,"E165.MirrorCS"),sQuery(id+"F0.wireOp",EDGE,"E166.MirrorCS"),sQuery(id+"F0.wireOp",EDGE,"E167.MirrorCS"),sQuery(id+"F0.wireOp",EDGE,"E168.MirrorCS"),sQuery(id+"F0.wireOp",EDGE,"E169.MirrorC"),sQuery(id+"F0.wireOp",EDGE,"E170.MirrorCS"),sQuery(id+"F0.wireOp",EDGE,"E171.MirrorCS"),sQuery(id+"F0.wireOp",EDGE,"E172.MirrorCS"),sQuery(id+"F0.wireOp",EDGE,"E173.MirrorCS"),sQuery(id+"F0.wireOp",EDGE,"E175.MirrorCS"),sQuery(id+"F0.wireOp",EDGE,"E176.MirrorCS"),sQuery(id+"F0.wireOp",EDGE,"E177.MirrorCS"),sQuery(id+"F0.wireOp",EDGE,"E178.MirrorCS"),sQuery(id+"F0.wireOp",EDGE,"E179.MirrorCS"),sQuery(id+"F0.wireOp",EDGE,"E180.MirrorCS"),sQuery(id+"F0.wireOp",EDGE,"E181.MirrorCS"),sQuery(id+"F0.wireOp",EDGE,"E183.MirrorCS"),sQuery(id+"F0.wireOp",EDGE,"E184.MirrorCS"),sQuery(id+"F0.wireOp",EDGE,"E185.MirrorCS"),sQuery(id+"F0.wireOp",EDGE,"E186.MirrorCS"),sQuery(id+"F0.wireOp",EDGE,"E187.MirrorCS"),sQuery(id+"F0.wireOp",EDGE,"E188.MirrorCS"),sQuery(id+"F0.wireOp",EDGE,"E189.MirrorCS"),sQuery(id+"F0.wireOp",EDGE,"E150.MirrorCS"),sQuery(id+"F0.wireOp",EDGE,"E190.MirrorCS"),sQuery(id+"F0.wireOp",EDGE,"E152.MirrorCS"),sQuery(id+"F0.wireOp",EDGE,"E191.MirrorCS"),sQuery(id+"F0.wireOp",EDGE,"E192.MirrorCS"),sQuery(id+"F0.wireOp",EDGE,"E193.MirrorCS"),sQuery(id+"F0.wireOp",EDGE,"E194.MirrorCS"),sQuery(id+"F0.wireOp",EDGE,"E195.MirrorCS"),sQuery(id+"F0.wireOp",EDGE,"E196.MirrorCS"),sQuery(id+"F0.wireOp",EDGE,"E197.MirrorCS"),sQuery(id+"F0.wireOp",EDGE,"E153.MirrorCS"),sQuery(id+"F0.wireOp",EDGE,"E198.MirrorCS"),sQuery(id+"F0.wireOp",EDGE,"E149.MirrorCS"),sQuery(id+"F0.wireOp",EDGE,"E199.MirrorCS"),sQuery(id+"F0.wireOp",EDGE,"E200.MirrorCS")])]});
            var Q1;
            Q1=qCreatedBy(makeId("Origin.pointOp"),VERTEX);
            transform(context, id + "F2", {"entities" : qUnion([Q0]), "transformType" : TransformType.SCALE_UNIFORMLY, "scale" : 0.27, "scalePoint" : qUnion([Q1]), "makeCopy" : false});
        }
        {
            var Q0;
            Q0=makeQuery(id+"F1.opExtrude","SWEPT_EDGE",EDGE,{"disambiguationData":[OSD([sQuery(id+"F0.wireOp",EDGE,"E74"),sQuery(id+"F0.wireOp",EDGE,"E78.MirrorCS")])]});
            var Q1;
            Q1=makeQuery(id+"F1.opExtrude","SWEPT_EDGE",EDGE,{"disambiguationData":[OSD([sQuery(id+"F0.wireOp",EDGE,"E162.MirrorCS"),sQuery(id+"F0.wireOp",EDGE,"E189.MirrorCS")])]});
            var Q2;
            Q2=makeQuery(id+"F1.opExtrude","SWEPT_EDGE",EDGE,{"disambiguationData":[OSD([sQuery(id+"F0.wireOp",EDGE,"E84.MirrorCS"),sQuery(id+"F0.wireOp",EDGE,"E85.MirrorCS")])]});
            var Q3;
            Q3=makeQuery(id+"F1.opExtrude","SWEPT_EDGE",EDGE,{"disambiguationData":[OSD([sQuery(id+"F0.wireOp",EDGE,"E184.MirrorCS"),sQuery(id+"F0.wireOp",EDGE,"E200.MirrorCS")])]});
            fillet(context, id + "F3", {"entities" : qUnion([Q0, Q1, Q2, Q3]), "radius" : 3 * mm, "tangentPropagation" : true, "allowEdgeOverflow" : false});
        }
        {
            var Q0;
            Q0=makeQuery(id+"F1.opExtrude","SWEPT_EDGE",EDGE,{"disambiguationData":[OSD([sQuery(id+"F0.wireOp",EDGE,"E0"),sQuery(id+"F0.wireOp",EDGE,"E16.MirrorCS")])]});
            var Q1;
            Q1=makeQuery(id+"F1.opExtrude","SWEPT_EDGE",EDGE,{"disambiguationData":[OSD([sQuery(id+"F0.wireOp",EDGE,"E163.MirrorCS"),sQuery(id+"F0.wireOp",EDGE,"E183.MirrorCS")])]});
            var Q2;
            Q2=makeQuery(id+"F1.opExtrude","SWEPT_EDGE",EDGE,{"disambiguationData":[OSD([sQuery(id+"F0.wireOp",EDGE,"E150.MirrorCS"),sQuery(id+"F0.wireOp",EDGE,"E199.MirrorCS")])]});
            var Q3;
            Q3=makeQuery(id+"F1.opExtrude","SWEPT_EDGE",EDGE,{"disambiguationData":[OSD([sQuery(id+"F0.wireOp",EDGE,"E34.MirrorCS"),sQuery(id+"F0.wireOp",EDGE,"E32.MirrorCS")])]});
            fillet(context, id + "F4", {"entities" : qUnion([Q0, Q1, Q2, Q3]), "radius" : 4 * mm, "tangentPropagation" : true, "allowEdgeOverflow" : false});
        }
    });
